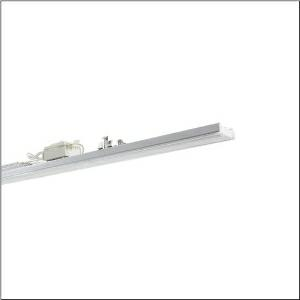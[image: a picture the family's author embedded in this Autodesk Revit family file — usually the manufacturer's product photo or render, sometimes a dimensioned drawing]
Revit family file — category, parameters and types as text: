
# Revit family: licross_r__21_recessed_mo_52te127n485g_14fa
name_source: partatom
category: Lighting Fixtures
units: mm (PartAtom-declared; Revit-internal decimal feet)

## family parameters
Cut with Voids When Loaded = No
Host = Face
Light Source = No
Part Type = Normal
Room Calculation Point = No
Round Connector Dimension = Use Diameter
Shared = No

## types (1)
- Licross® 21 Recessed MO (1 x LED, 8820 lm, 47.9 W, 4000K)
    Apparent Load = 48 VA
    CIE Flux Codes = 72 92 99 100 100
    Color Rendering = 80
    Color Temperature = 4000K
    Default Elevation = 1800 mm
    Description = Licross® 21 Recessed MO, luminaire insert, of sheet steel, galvanised, coil coated, white, length: 1.500mm, width: 66mm, height: 67mm, LED rated luminous flux: 8.820lm, light colour: 840, control gear: ON/OFF, with plug, 3-pole, with phase selection, mains connection: 220..240V, AC, 50/60Hz, rated input power: 48W, halogen-free wiring, primary optical cover: cover, of PMMA, light emission: direct distribution, primary light characteristic: symmetric, protection rating (complete): IP54, insulation class (complete): insulation class I (protective earthing), certification: CE, ENEC, VDE, UKCA, protection symbol: D if used in an environment with non-conductive dust loads with corresponding accessories, impact resistance: IK06, permissible ambient temperature for indoor applications: -35..+40°C, corresponds to IFS (International Featured Standards) requirements for safety and quality in the food industry, reducing of maximum allowable ambient temperature of 5°C with ceiling mounting, LABS conformity tested according to VDMA 24364:2018-05, packaging unit: 1 piece
    Height = 58 mm
    Lamp = 1 x LED
    Lamp Light Flux = 8820 lm
    Lamp Power = 47.9 W
    Lamp count = 1
    Length = 1500 mm
    Luminous efficacy = 184 lm/W
    Manufacturer = Siteco
    ModVariant = No
    Model = 52TE127N485G
    Mounting Place = Ceiling
    Mounting Type = Pendant
    Number of Poles = 1
    OnlyDefault = Yes
    Power Factor = 1
    Product Name = Licross® 21 Recessed MO
    Product group = luminaire insert
    ProductGroupID = 902
    Protection Class = Protection class I
    Protection Degree = IP 54
    RLX_Detail_Level = 1
    RLX_Emergency_Light_Flux = 0 lm
    RLX_Emergency_Type = 0
    RLX_Emergency_Type_DB = No
    RlxData = <blob elided: 20897 chars, md5=6419cf5e>
    Socket = socket
    Standby Power = 0 W
    System Light Flux = 8820 lm
    System Power = 48 W
    Type Comments = Product without accessories
    Type Image = l_1296930.jpg
    URL = http://relux.com
    VarID = ---
    Voltage = 0 V
    Weight = 0.00 kg
    Width = 66 mm

## geometry (parser evidence)
native form markers: Blend x4, Sweep x13
no freeform markers — native parametric forms only
